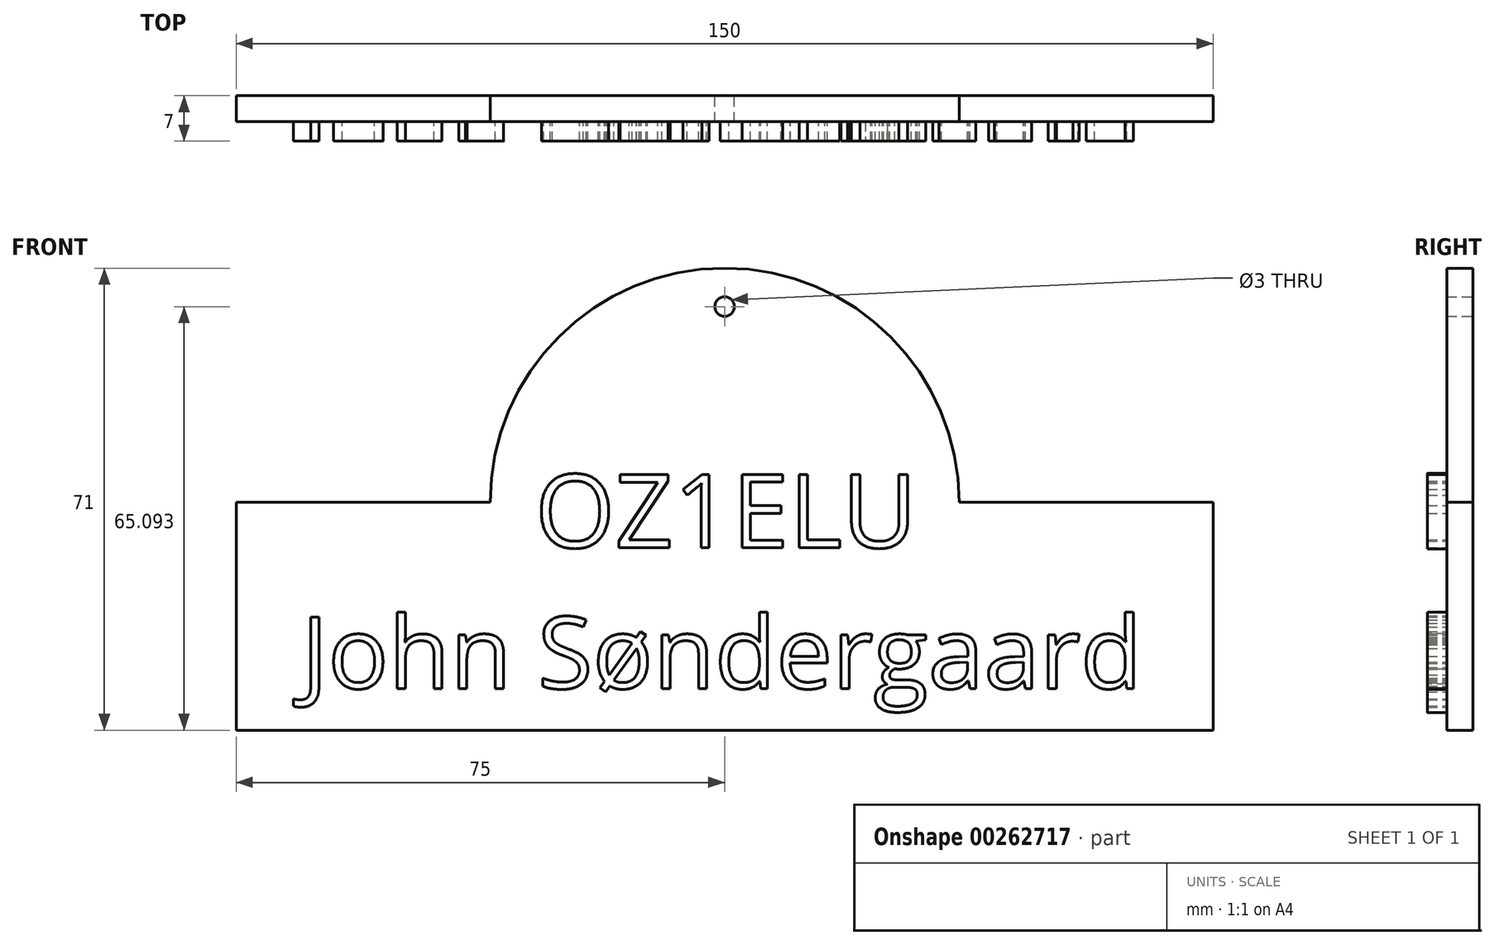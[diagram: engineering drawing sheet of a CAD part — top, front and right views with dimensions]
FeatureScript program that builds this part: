
annotation { "Feature Type Name" : "Feature", "Feature Type Description" : "" }
export const myFeature = defineFeature(function(context is Context, id is Id, definition is map)
    precondition{}
    {
        {
            var Q0;
            Q0=qCreatedBy(makeId("Front.planeOp"),FACE);
            var sketch = newSketch(context, id + "F0", { "sketchPlane" : qUnion([Q0])});
            skLineSegment(sketch, "E0.bottom", {"start": v(-75, -17.5) * mm, "end": v(75, -17.5) * mm});
            skLineSegment(sketch, "E0.top", {"start": v(-75, 17.5) * mm, "end": v(-36, 17.5) * mm});
            skLineSegment(sketch, "E0.left", {"start": v(-75, -17.5) * mm, "end": v(-75, 17.5) * mm});
            skLineSegment(sketch, "E0.right", {"start": v(75, -17.5) * mm, "end": v(75, 17.5) * mm});
            skPoint(sketch, "E0.middle", {"position": v(0, 0) * mm});
            skArc(sketch, "E1", {"start": v(-36, 17.5) * mm, "mid": v(0, 53.5) * mm, "end": v(36, 17.5) * mm});
            skLineSegment(sketch, "E2.trimOffspring", {"start": v(36, 17.5) * mm, "end": v(75, 17.5) * mm});
            skCircle(sketch, "E3", {"center": v(0, 47.6) * mm, "radius": 1.5 * mm});
            skText(sketch, "E4", { "text": "John Søndergaard", "fontName": "OpenSans-Regular.ttf"});
            skText(sketch, "E5", { "text": "OZ1ELU", "fontName": "NotoSerif-Bold.ttf"});
            skPoint(sketch, "E6", {"position": v(0, -17.5) * mm});
            const initialGuessF0  = {"E4": [-0.07038, -0.06316, 1, 0, 0.012], "E5": [-0.02857, -0.03614, 1, 0, 0.01]};
            skSetInitialGuess(sketch, initialGuessF0);
            skSolve(sketch);
        }
        {
            var Q0;
            Q0=makeQuery(id+"F0.imprint","IMPRINT",FACE,{"disambiguationData":[TD([[makeQuery(id+"F0.imprint","IMPRINT",EDGE,{"derivedFrom":sQuery(id+"F0.wireOp",EDGE,"E0.bottom")}),1.0]])]});
            extrude(context, id + "F1", {"entities" : qUnion([Q0]), "depth" : 4 * mm});
        }
        {
            var Q0;
            Q0=makeQuery(id+"F1.opExtrude","CAP_FACE",FACE,{"disambiguationData":[OSD([sQuery(id+"F0.wireOp",EDGE,"E0.bottom"),sQuery(id+"F0.wireOp",EDGE,"E0.top"),sQuery(id+"F0.wireOp",EDGE,"E0.left"),sQuery(id+"F0.wireOp",EDGE,"E0.right"),sQuery(id+"F0.wireOp",EDGE,"E1"),sQuery(id+"F0.wireOp",EDGE,"E2.trimOffspring"),sQuery(id+"F0.wireOp",EDGE,"E3")])],"isStart":false});
            var sketch = newSketch(context, id + "F2", { "sketchPlane" : qUnion([Q0])});
            skText(sketch, "E7", { "text": "John Søndergaard", "fontName": "OpenSans-Regular.ttf"});
            skText(sketch, "E8", { "text": "OZ1ELU", "fontName": "OpenSans-Regular.ttf"});
            const initialGuessF2  = {"E7": [-0.065, -0.01108, 1, 0, 0.01108], "E8": [-0.0291, 0.01054, 1, 0, 0.01133]};
            skSetInitialGuess(sketch, initialGuessF2);
            skSolve(sketch);
        }
        {
            var Q0;
            Q0 = qSketchRegion(id + "F2", true);
            extrude(context, id + "F3", {"entities" : qUnion([Q0]), "operationType" : NewBodyOperationType.ADD, "depth" : 3 * mm});
        }
    });
